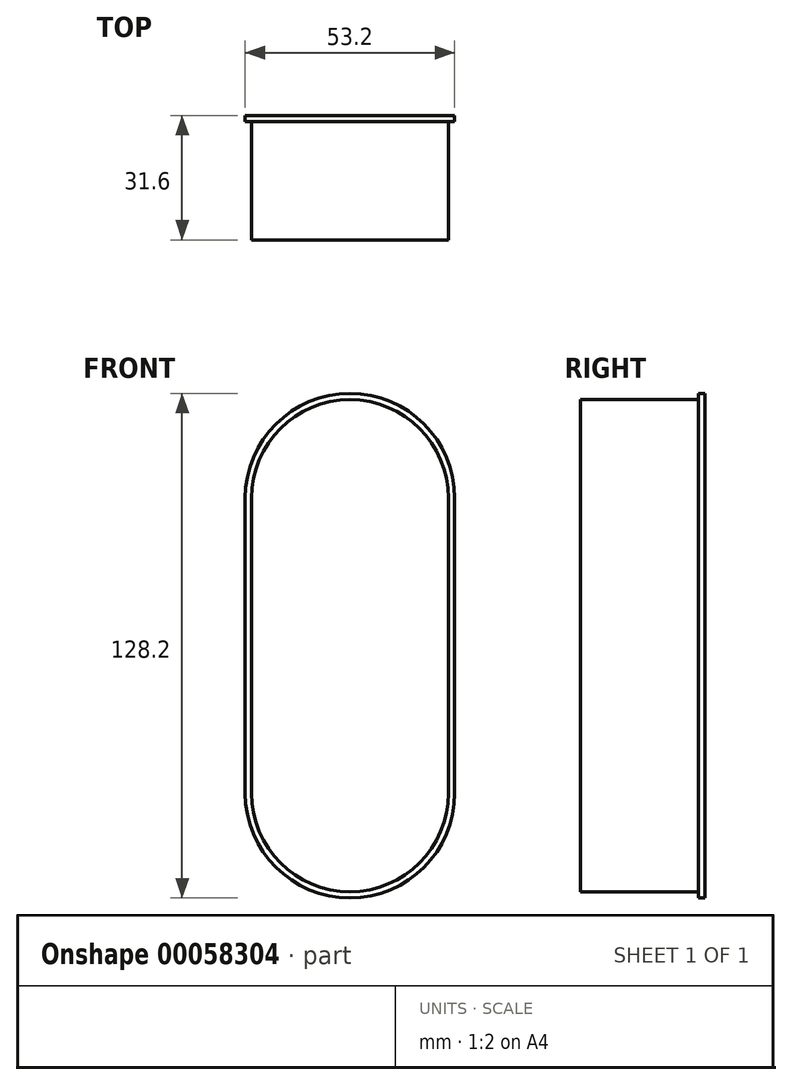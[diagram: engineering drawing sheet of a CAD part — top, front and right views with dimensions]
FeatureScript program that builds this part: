
annotation { "Feature Type Name" : "Feature", "Feature Type Description" : "" }
export const myFeature = defineFeature(function(context is Context, id is Id, definition is map)
    precondition{}
    {
        {
            assignVariable(context, id + "F0", {"name" : "height", "anyValue" : 30});
        }
        {
            assignVariable(context, id + "F1", {"name" : "wall", "anyValue" : 1.6});
        }
        {
            var Q0;
            Q0=qCreatedBy(makeId("Front.planeOp"),FACE);
            var sketch = newSketch(context, id + "F2", { "sketchPlane" : qUnion([Q0])});
            skLineSegment(sketch, "E0", {"start": v(0, 0) * mm, "end": v(0, 75) * mm, "construction": true});
            skArc(sketch, "E1.0.startCap", {"start": v(25, 0) * mm, "mid": v(0, -25) * mm, "end": v(-25, 0) * mm});
            skArc(sketch, "E1.0.endCap", {"start": v(-25, 75) * mm, "mid": v(0, 100) * mm, "end": v(25, 75) * mm});
            skLineSegment(sketch, "E1.0.left", {"start": v(-25, 0) * mm, "end": v(-25, 75) * mm});
            skLineSegment(sketch, "E1.0.right", {"start": v(25, 0) * mm, "end": v(25, 75) * mm});
            skArc(sketch, "E2.0", {"start": v(-26.6, 75) * mm, "mid": v(0, 101.6) * mm, "end": v(26.6, 75) * mm});
            skLineSegment(sketch, "E2.1", {"start": v(-26.6, 0) * mm, "end": v(-26.6, 75) * mm});
            skArc(sketch, "E2.2", {"start": v(26.6, 0) * mm, "mid": v(0, -26.6) * mm, "end": v(-26.6, 0) * mm});
            skLineSegment(sketch, "E2.3", {"start": v(26.6, 0) * mm, "end": v(26.6, 75) * mm});
            skSolve(sketch);
        }
        {
            var Q0;
            Q0=makeQuery(id+"F2.imprint","IMPRINT",FACE,{"disambiguationData":[TD([[makeQuery(id+"F2.imprint","IMPRINT",EDGE,{"derivedFrom":sQuery(id+"F2.wireOp",EDGE,"E1.0.startCap")}),1.0]])]});
            extrude(context, id + "F3", {"entities" : qUnion([Q0]), "depth" : (getVariable(context, 'height')) * mm});
        }
        {
            var Q0;
            Q0=makeQuery(id+"F2.imprint","IMPRINT",FACE,{"disambiguationData":[TD([[makeQuery(id+"F2.imprint","IMPRINT",EDGE,{"derivedFrom":sQuery(id+"F2.wireOp",EDGE,"E1.0.startCap")}),-1.0]])]});
            var Q1;
            Q1=makeQuery(id+"F2.imprint","IMPRINT",FACE,{"disambiguationData":[TD([[makeQuery(id+"F2.imprint","IMPRINT",EDGE,{"derivedFrom":sQuery(id+"F2.wireOp",EDGE,"E1.0.startCap")}),1.0]])]});
            extrude(context, id + "F4", {"entities" : qUnion([Q0, Q1]), "operationType" : NewBodyOperationType.ADD, "oppositeDirection" : true, "depth" : (getVariable(context, 'wall')) * mm});
        }
    });
